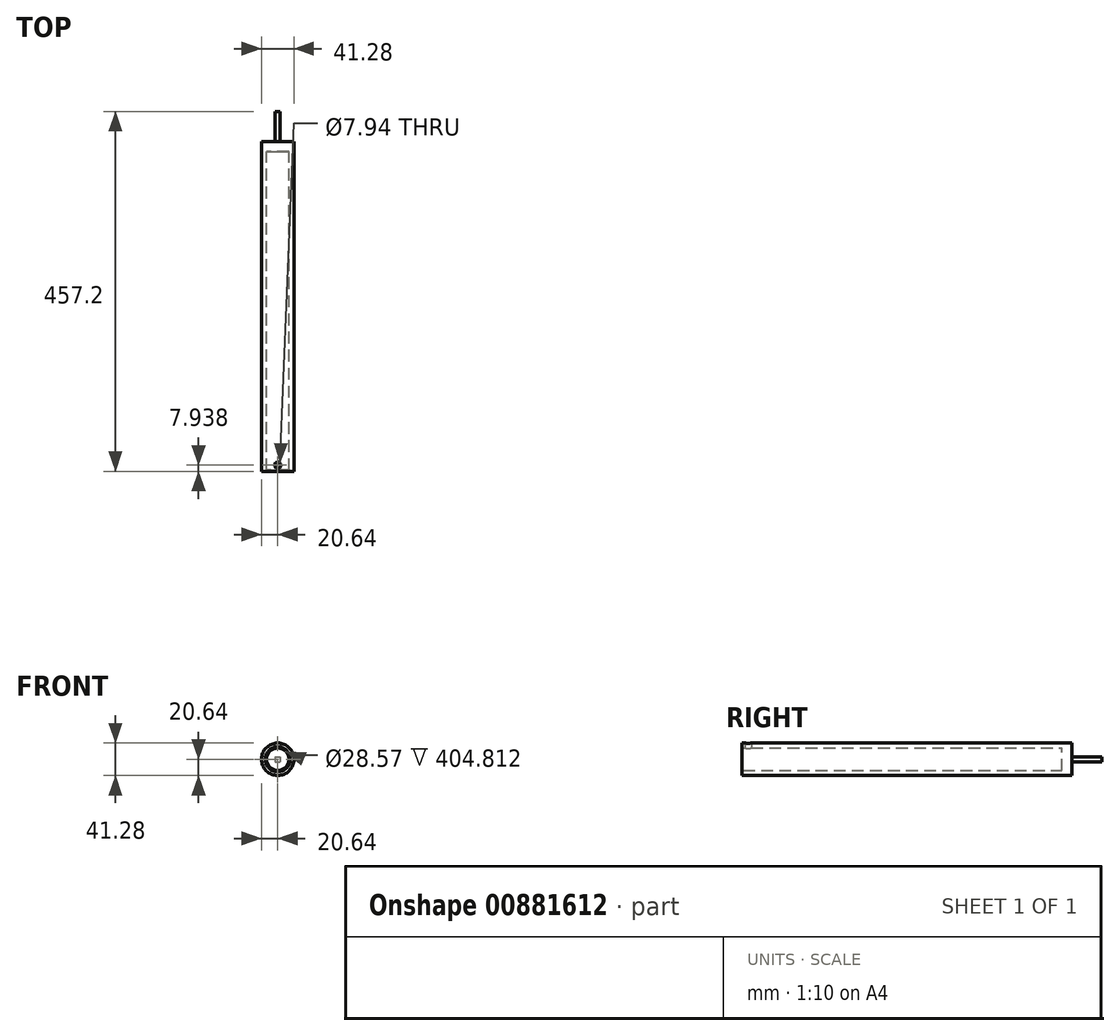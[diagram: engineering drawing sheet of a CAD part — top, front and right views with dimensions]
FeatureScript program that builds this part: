
annotation { "Feature Type Name" : "Feature", "Feature Type Description" : "" }
export const myFeature = defineFeature(function(context is Context, id is Id, definition is map)
    precondition{}
    {
        {
            var Q0;
            Q0=qCreatedBy(makeId("Front.planeOp"),FACE);
            var sketch = newSketch(context, id + "F0", { "sketchPlane" : qUnion([Q0])});
            skCircle(sketch, "E0", {"center": v(0, 0) * mm, "radius": 20.64 * mm});
            skCircle(sketch, "E1", {"center": v(0, 0) * mm, "radius": 14.29 * mm});
            skSolve(sketch);
        }
        {
            var Q0;
            Q0 = qSketchRegion(id + "F0", true);
            extrude(context, id + "F1", {"entities" : qUnion([Q0]), "depth" : 406.4 * mm, "offsetDistance" : 25.4 * mm});
        }
        {
            var Q0;
            Q0=makeQuery(id+"F1.opExtrude","CAP_FACE",FACE,{"disambiguationData":[OSD([sQuery(id+"F0.wireOp",EDGE,"E0"),sQuery(id+"F0.wireOp",EDGE,"E1")])],"isStart":true});
            var sketch = newSketch(context, id + "F2", { "sketchPlane" : qUnion([Q0])});
            skCircle(sketch, "E2", {"center": v(0, 0) * mm, "radius": 20.64 * mm});
            skSolve(sketch);
        }
        {
            var Q0;
            Q0 = qSketchRegion(id + "F2", true);
            extrude(context, id + "F3", {"entities" : qUnion([Q0]), "operationType" : NewBodyOperationType.ADD, "depth" : 12.7 * mm, "offsetDistance" : 25.4 * mm});
        }
        {
            var Q0;
            Q0=makeQuery(id+"F3.opExtrude","CAP_FACE",FACE,{"disambiguationData":[OSD([sQuery(id+"F2.wireOp",EDGE,"E2")])],"isStart":false});
            var sketch = newSketch(context, id + "F4", { "sketchPlane" : qUnion([Q0])});
            skLineSegment(sketch, "E3.bottom", {"start": v(3.18, 3.18) * mm, "end": v(-3.17, 3.18) * mm});
            skLineSegment(sketch, "E3.top", {"start": v(3.17, -3.17) * mm, "end": v(-3.18, -3.17) * mm});
            skLineSegment(sketch, "E3.left", {"start": v(3.18, 3.18) * mm, "end": v(3.17, -3.17) * mm});
            skLineSegment(sketch, "E3.right", {"start": v(-3.17, 3.18) * mm, "end": v(-3.18, -3.17) * mm});
            skPoint(sketch, "E3.middle", {"position": v(0, 0) * mm});
            skSolve(sketch);
        }
        {
            var Q0;
            Q0 = qSketchRegion(id + "F4", true);
            extrude(context, id + "F5", {"entities" : qUnion([Q0]), "operationType" : NewBodyOperationType.ADD, "depth" : 38.1 * mm, "offsetDistance" : 25.4 * mm});
        }
        {
            var Q0;
            Q0=qCreatedBy(makeId("Top.planeOp"),FACE);
            var sketch = newSketch(context, id + "F6", { "sketchPlane" : qUnion([Q0])});
            skLineSegment(sketch, "E4", {"start": v(0, 0) * mm, "end": v(0, -398.46) * mm});
            skCircle(sketch, "E5", {"center": v(0, -398.46) * mm, "radius": 3.97 * mm});
            skSolve(sketch);
        }
        {
            var Q0;
            Q0 = qSketchRegion(id + "F6", true);
            extrude(context, id + "F7", {"entities" : qUnion([Q0]), "operationType" : NewBodyOperationType.REMOVE, "depth" : 25.4 * mm, "offsetDistance" : 25.4 * mm});
        }
        {
            var Q0;
            Q0=makeQuery(id+"F1.opExtrude","CAP_EDGE",EDGE,{"disambiguationData":[OSD([sQuery(id+"F0.wireOp",EDGE,"E1")])],"isStart":false});
            chamfer(context, id + "F8", {"entities" : qUnion([Q0]), "width" : 1.59 * mm, "tangentPropagation" : true});
        }
    });
